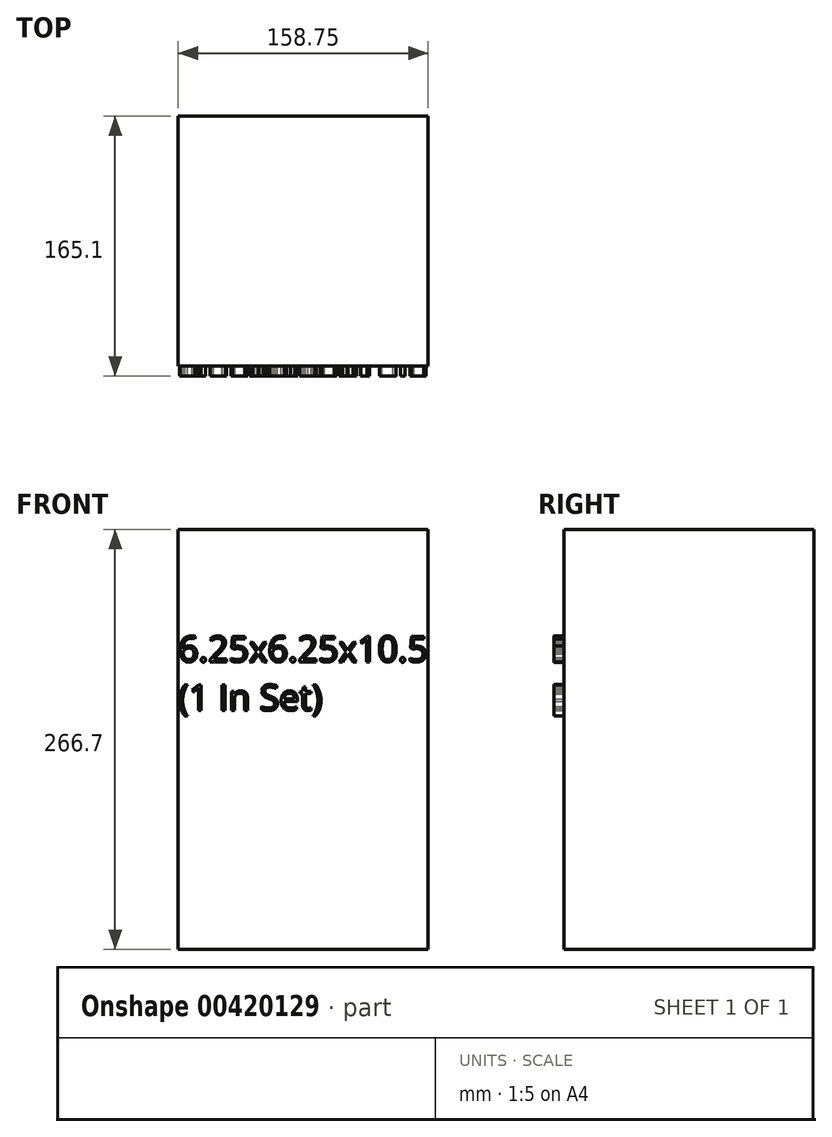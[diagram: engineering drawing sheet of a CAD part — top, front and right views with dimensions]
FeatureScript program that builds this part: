
annotation { "Feature Type Name" : "Feature", "Feature Type Description" : "" }
export const myFeature = defineFeature(function(context is Context, id is Id, definition is map)
    precondition{}
    {
        {
            var Q0;
            Q0=qCreatedBy(makeId("Front.planeOp"),FACE);
            var sketch = newSketch(context, id + "F0", { "sketchPlane" : qUnion([Q0])});
            skLineSegment(sketch, "E0.bottom", {"start": v(0, 0) * mm, "end": v(158.75, 0) * mm});
            skLineSegment(sketch, "E0.top", {"start": v(0, 266.7) * mm, "end": v(158.75, 266.7) * mm});
            skLineSegment(sketch, "E0.left", {"start": v(0, 0) * mm, "end": v(0, 266.7) * mm});
            skLineSegment(sketch, "E0.right", {"start": v(158.75, 0) * mm, "end": v(158.75, 266.7) * mm});
            skSolve(sketch);
        }
        {
            var Q0;
            Q0=makeQuery(id+"F0.imprint","IMPRINT",FACE,{"disambiguationData":[TD([[makeQuery(id+"F0.imprint","IMPRINT",EDGE,{"derivedFrom":sQuery(id+"F0.wireOp",EDGE,"E0.bottom")}),1.0]])]});
            extrude(context, id + "F1", {"entities" : qUnion([Q0]), "depth" : 158.75 * mm});
        }
        {
            var Q0;
            Q0=makeQuery(id+"F1.opExtrude","CAP_FACE",FACE,{"disambiguationData":[OSD([sQuery(id+"F0.wireOp",EDGE,"E0.bottom"),sQuery(id+"F0.wireOp",EDGE,"E0.top"),sQuery(id+"F0.wireOp",EDGE,"E0.left"),sQuery(id+"F0.wireOp",EDGE,"E0.right")])],"isStart":false});
            var sketch = newSketch(context, id + "F2", { "sketchPlane" : qUnion([Q0])});
            skText(sketch, "E1", { "text": "6.25x6.25x10.5\n(1 In Set)", "fontName": "OpenSans-Regular.ttf"});
            const initialGuessF2  = {"E1": [0, 0.18272, 1, 0, 0.01633]};
            skSetInitialGuess(sketch, initialGuessF2);
            skSolve(sketch);
        }
        {
            var Q0;
            Q0 = qSketchRegion(id + "F2", true);
            extrude(context, id + "F3", {"entities" : qUnion([Q0]), "operationType" : NewBodyOperationType.ADD, "depth" : 6.35 * mm});
        }
    });
